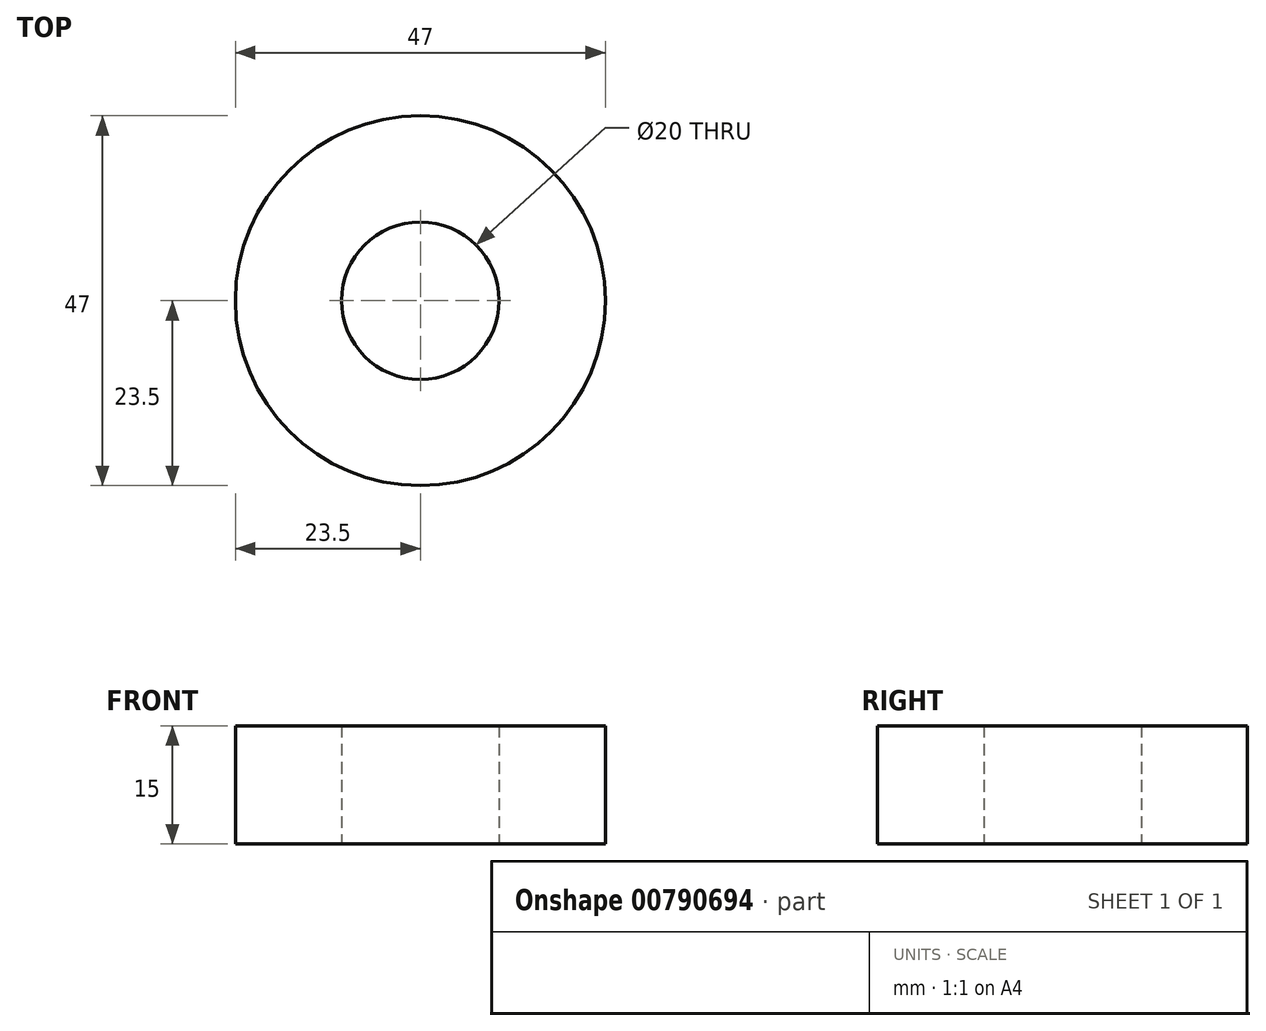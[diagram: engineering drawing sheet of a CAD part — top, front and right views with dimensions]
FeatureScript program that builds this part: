
annotation { "Feature Type Name" : "Feature", "Feature Type Description" : "" }
export const myFeature = defineFeature(function(context is Context, id is Id, definition is map)
    precondition{}
    {
        {
            var Q0;
            Q0=qCreatedBy(makeId("Top.planeOp"),FACE);
            var sketch = newSketch(context, id + "F0", { "sketchPlane" : qUnion([Q0])});
            skCircle(sketch, "E0", {"center": v(0, 0) * mm, "radius": 23.5 * mm});
            skCircle(sketch, "E1", {"center": v(0, 0) * mm, "radius": 10 * mm});
            skSolve(sketch);
        }
        {
            var Q0;
            Q0=makeQuery(id+"F0.imprint","IMPRINT",FACE,{"disambiguationData":[TD([[makeQuery(id+"F0.imprint","IMPRINT",EDGE,{"derivedFrom":sQuery(id+"F0.wireOp",EDGE,"E0")}),1.0]])]});
            extrude(context, id + "F1", {"entities" : qUnion([Q0]), "depth" : 15 * mm, "offsetDistance" : 25 * mm});
        }
    });
